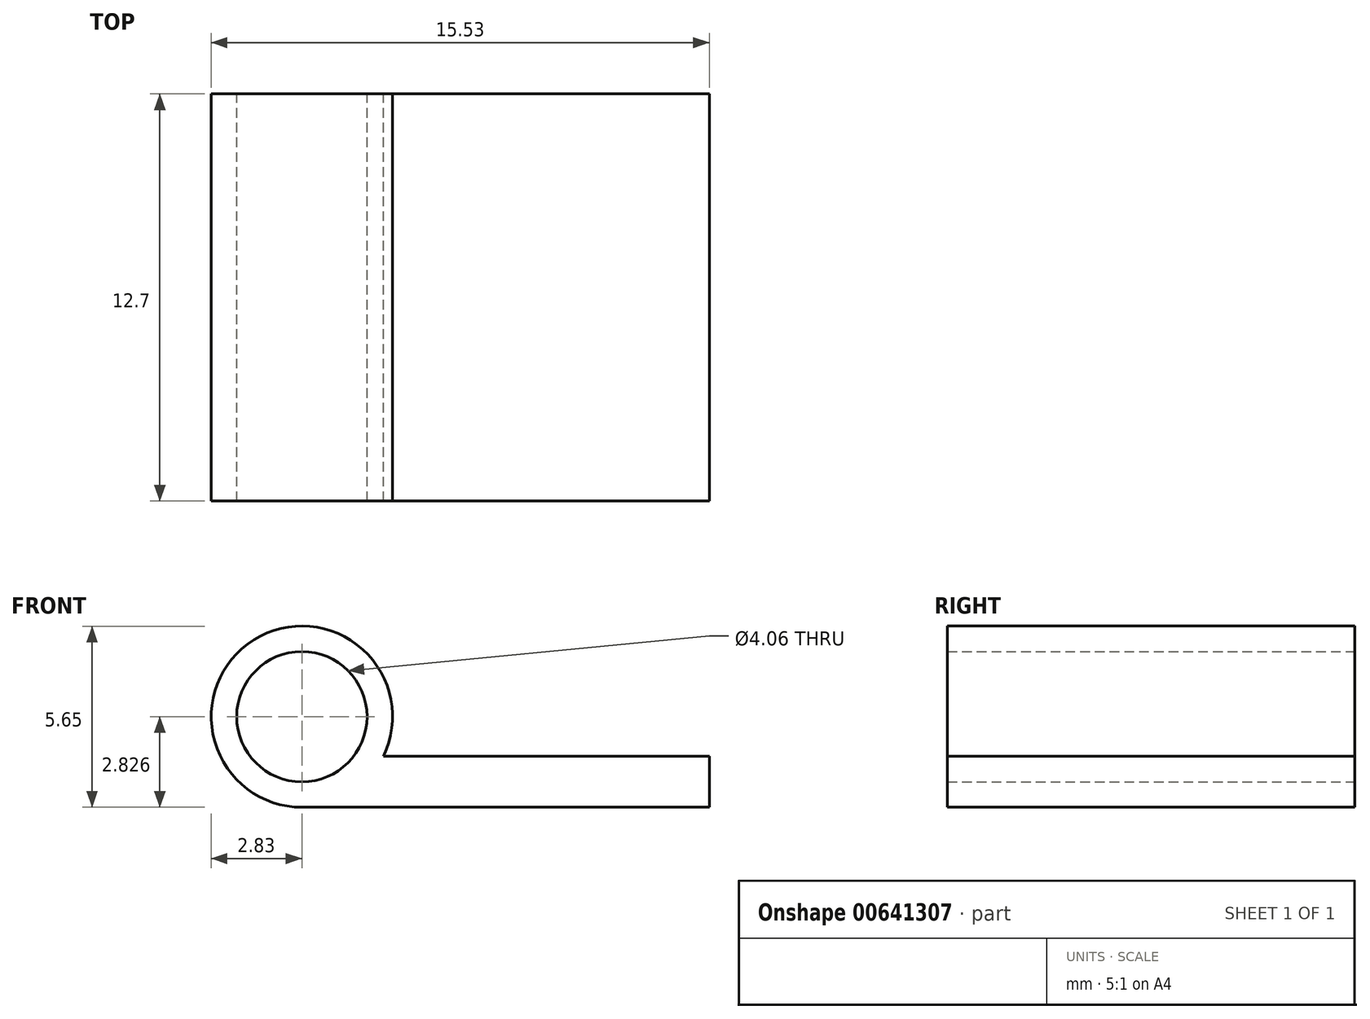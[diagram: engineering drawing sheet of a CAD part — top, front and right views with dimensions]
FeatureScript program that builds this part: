
annotation { "Feature Type Name" : "Feature", "Feature Type Description" : "" }
export const myFeature = defineFeature(function(context is Context, id is Id, definition is map)
    precondition{}
    {
        {
            var Q0;
            Q0=qCreatedBy(makeId("Front.planeOp"),FACE);
            var sketch = newSketch(context, id + "F0", { "sketchPlane" : qUnion([Q0])});
            skLineSegment(sketch, "E0.bottom", {"start": v(0, 0) * mm, "end": v(12.7, 0) * mm});
            skLineSegment(sketch, "E0.top", {"start": v(2.54, 1.59) * mm, "end": v(12.7, 1.59) * mm});
            skLineSegment(sketch, "E0.right", {"start": v(12.7, 0) * mm, "end": v(12.7, 1.59) * mm});
            skArc(sketch, "E1", {"start": v(2.54, 1.59) * mm, "mid": v(-1.5, 5.22) * mm, "end": v(0, 0) * mm});
            skPoint(sketch, "E1.second.point", {"position": v(0, 5.65) * mm});
            skPoint(sketch, "E1.third.point", {"position": v(-2.75, 3.45) * mm});
            skCircle(sketch, "E2", {"center": v(0, 2.83) * mm, "radius": 2.03 * mm});
            skSolve(sketch);
        }
        {
            var Q0;
            Q0 = qSketchRegion(id + "F0", true);
            extrude(context, id + "F1", {"entities" : qUnion([Q0]), "depth" : 12.7 * mm, "offsetDistance" : 25.4 * mm});
        }
    });
